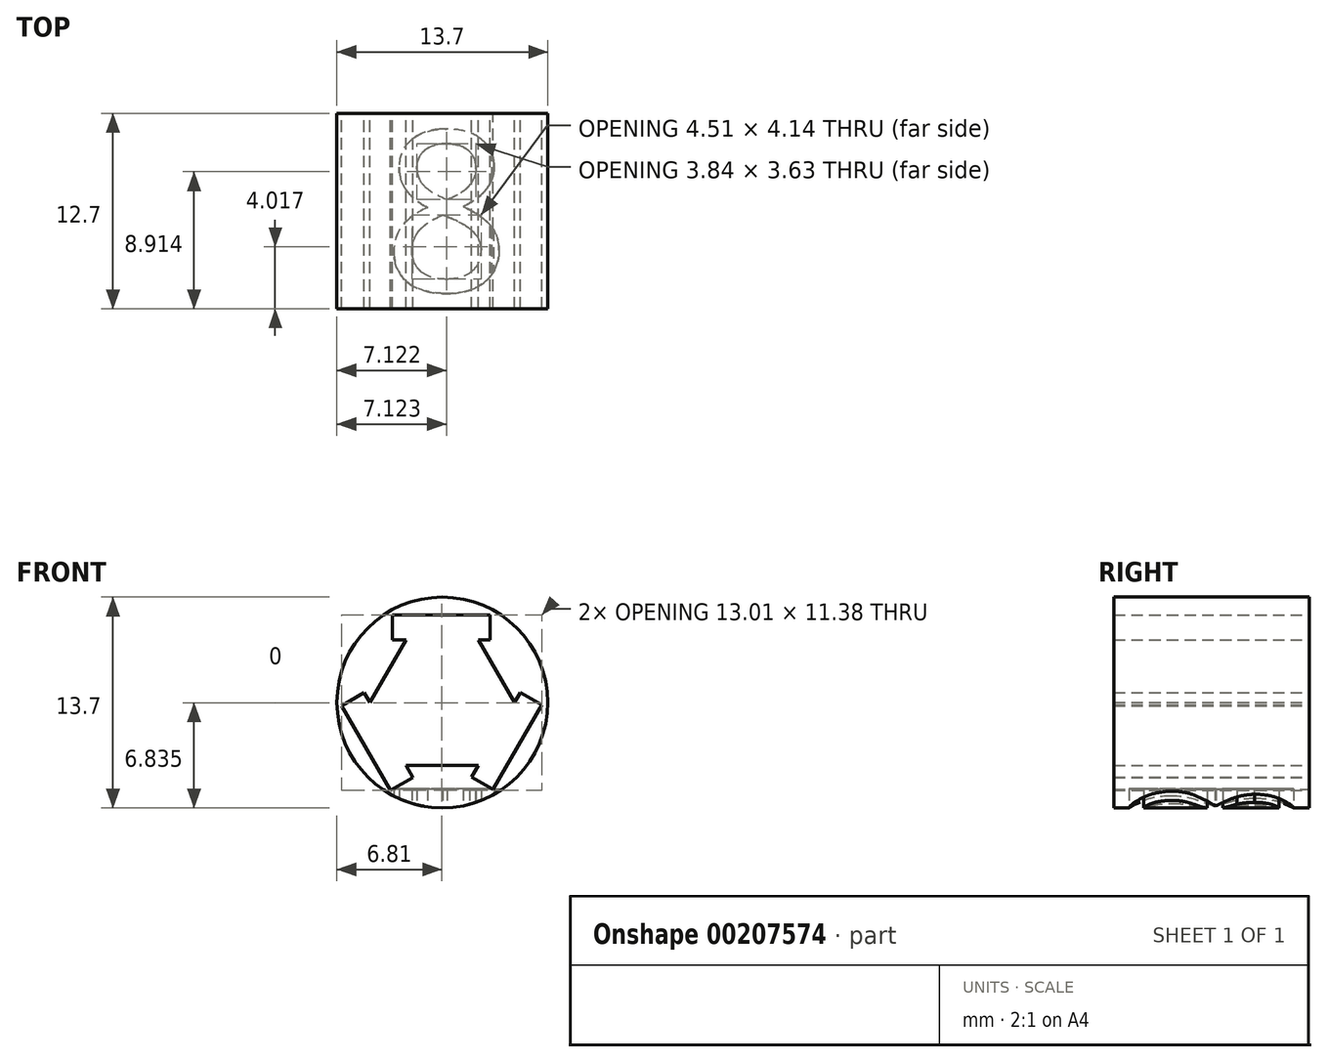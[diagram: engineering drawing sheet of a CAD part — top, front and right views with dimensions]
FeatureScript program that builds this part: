
annotation { "Feature Type Name" : "Feature", "Feature Type Description" : "" }
export const myFeature = defineFeature(function(context is Context, id is Id, definition is map)
    precondition{}
    {
        {
            var Q0;
            Q0=qCreatedBy(makeId("Front.planeOp"),FACE);
            var sketch = newSketch(context, id + "F0", { "sketchPlane" : qUnion([Q0])});
            skCircle(sketch, "E0.cCircle", {"center": v(0, 0) * mm, "radius": 4.08 * mm, "construction": true});
            skLineSegment(sketch, "E0.0", {"start": v(4.7, 0) * mm, "end": v(2.35, -4.08) * mm});
            skLineSegment(sketch, "E0.1", {"start": v(2.35, -4.08) * mm, "end": v(-2.35, -4.08) * mm});
            skLineSegment(sketch, "E0.2", {"start": v(-2.35, -4.07) * mm, "end": v(-4.7, 0) * mm});
            skLineSegment(sketch, "E0.3", {"start": v(-4.7, 0) * mm, "end": v(-2.35, 4.07) * mm});
            skLineSegment(sketch, "E0.4", {"start": v(-2.35, 4.08) * mm, "end": v(2.35, 4.08) * mm});
            skLineSegment(sketch, "E0.5", {"start": v(2.35, 4.07) * mm, "end": v(4.7, 0) * mm});
            skPoint(sketch, "E0.0.midPoint", {"position": v(3.53, -2.04) * mm});
            skLineSegment(sketch, "E1", {"start": v(0, 4.08) * mm, "end": v(0, -4.08) * mm, "construction": true});
            skCircle(sketch, "E2", {"center": v(0, 0) * mm, "radius": 6.85 * mm});
            skLineSegment(sketch, "E3", {"start": v(0, 4.07) * mm, "end": v(-1.61, 4.07) * mm});
            skLineSegment(sketch, "E4", {"start": v(-3.24, 4.07) * mm, "end": v(-3.24, 5.68) * mm});
            skLineSegment(sketch, "E5", {"start": v(-3.24, 5.68) * mm, "end": v(3.1, 5.68) * mm});
            skLineSegment(sketch, "E6", {"start": v(3.1, 5.68) * mm, "end": v(3.1, 4.08) * mm});
            skLineSegment(sketch, "E7", {"start": v(1.82, 4.08) * mm, "end": v(0, 4.08) * mm});
            skLineSegment(sketch, "E8", {"start": v(-3.18, -2.64) * mm, "end": v(-2.35, -4.07) * mm});
            skLineSegment(sketch, "E9", {"start": v(-3.37, -5.7) * mm, "end": v(-6.55, -0.2) * mm});
            skLineSegment(sketch, "E10", {"start": v(-6.55, -0.2) * mm, "end": v(-5.08, 0.64) * mm});
            skLineSegment(sketch, "E11", {"start": v(-4.37, -0.57) * mm, "end": v(-3.18, -2.64) * mm});
            skLineSegment(sketch, "E12.0", {"start": v(-3.18, -2.64) * mm, "end": v(-4.35, -0.61) * mm, "construction": true});
            skLineSegment(sketch, "E13", {"start": v(3.53, -2.04) * mm, "end": v(4.34, -0.64) * mm});
            skLineSegment(sketch, "E14", {"start": v(5.08, 0.65) * mm, "end": v(6.47, -0.15) * mm});
            skLineSegment(sketch, "E15", {"start": v(6.47, -0.15) * mm, "end": v(3.3, -5.65) * mm});
            skLineSegment(sketch, "E16", {"start": v(3.3, -5.65) * mm, "end": v(1.9, -4.85) * mm});
            skLineSegment(sketch, "E17", {"start": v(1.9, -4.85) * mm, "end": v(3.53, -2.04) * mm});
            skLineSegment(sketch, "E18", {"start": v(-3.18, -2.64) * mm, "end": v(-3.18, -2.64) * mm});
            skLineSegment(sketch, "E19", {"start": v(3.53, -2.04) * mm, "end": v(3.53, -2.04) * mm});
            skLineSegment(sketch, "E20", {"start": v(0, 4.08) * mm, "end": v(0, 4.08) * mm});
            skLineSegment(sketch, "E21", {"start": v(-3.24, 4.07) * mm, "end": v(-2.35, 4.07) * mm});
            skLineSegment(sketch, "E22", {"start": v(2.35, 4.07) * mm, "end": v(3.1, 4.08) * mm});
            skLineSegment(sketch, "E23", {"start": v(-4.7, 0) * mm, "end": v(-5.08, 0.64) * mm});
            skLineSegment(sketch, "E24", {"start": v(4.7, 0) * mm, "end": v(5.08, 0.65) * mm});
            skLineSegment(sketch, "E25", {"start": v(-3.37, -5.7) * mm, "end": v(-1.92, -4.87) * mm});
            skLineSegment(sketch, "E26", {"start": v(-1.92, -4.87) * mm, "end": v(-2.35, -4.08) * mm});
            skLineSegment(sketch, "E27", {"start": v(-4.7, 0) * mm, "end": v(4.7, 0) * mm, "construction": true});
            skSolve(sketch);
        }
        {
            var Q0;
            {var subQ0=sQuery(id+"F0.wireOp",EDGE,"E0.1");Q0=makeQuery(id+"F0.imprint","IMPRINT",FACE,{"disambiguationData":[TD([[makeQuery(id+"F0.imprint","IMPRINT",EDGE,{"derivedFrom":subQ0}),1.0]])]});}
            extrude(context, id + "F1", {"entities" : qUnion([Q0]), "depth" : 12.7 * mm});
        }
        {
            var Q0;
            Q0=makeQuery(id+"F1.opExtrude","SWEPT_BODY",BODY,{"disambiguationData":[OSD([sQuery(id+"F0.wireOp",EDGE,"E0.0"),sQuery(id+"F0.wireOp",EDGE,"E0.1"),sQuery(id+"F0.wireOp",EDGE,"E0.2"),sQuery(id+"F0.wireOp",EDGE,"E0.3"),sQuery(id+"F0.wireOp",EDGE,"E0.4"),sQuery(id+"F0.wireOp",EDGE,"E0.5"),sQuery(id+"F0.wireOp",EDGE,"E2")])]});
            transform(context, id + "F2", {"entities" : qUnion([Q0]), "transformType" : TransformType.TRANSLATION_3D, "dx" : 0 * mm, "dy" : 0 * mm, "dz" : 0 * mm, "makeCopy" : true});
        }
        {
            var Q0;
            Q0=qCreatedBy(makeId("Top.planeOp"),FACE);
            cPlane(context, id + "F3", {"entities" : qUnion([Q0]), "cplaneType" : CPlaneType.OFFSET, "offset" : 7.11 * mm, "oppositeDirection" : true, "width" : 152.4 * mm, "height" : 152.4 * mm});
        }
        {
            var Q0;
            Q0=qCreatedBy(id+"F3.planeOp",FACE);
            var sketch = newSketch(context, id + "F4", { "sketchPlane" : qUnion([Q0])});
            skText(sketch, "E28", { "text": "8", "fontName": "OpenSans-Regular.ttf"});
            const initialGuessF4  = {"E28": [-0.00389, -0.01157, 1, 0, 0.0105]};
            skSetInitialGuess(sketch, initialGuessF4);
            skSolve(sketch);
        }
        {
            var Q0;
            Q0 = qSketchRegion(id + "F4", true);
            extrude(context, id + "F5", {"entities" : qUnion([Q0]), "operationType" : NewBodyOperationType.REMOVE, "depth" : 1.5 * mm});
        }
    });
